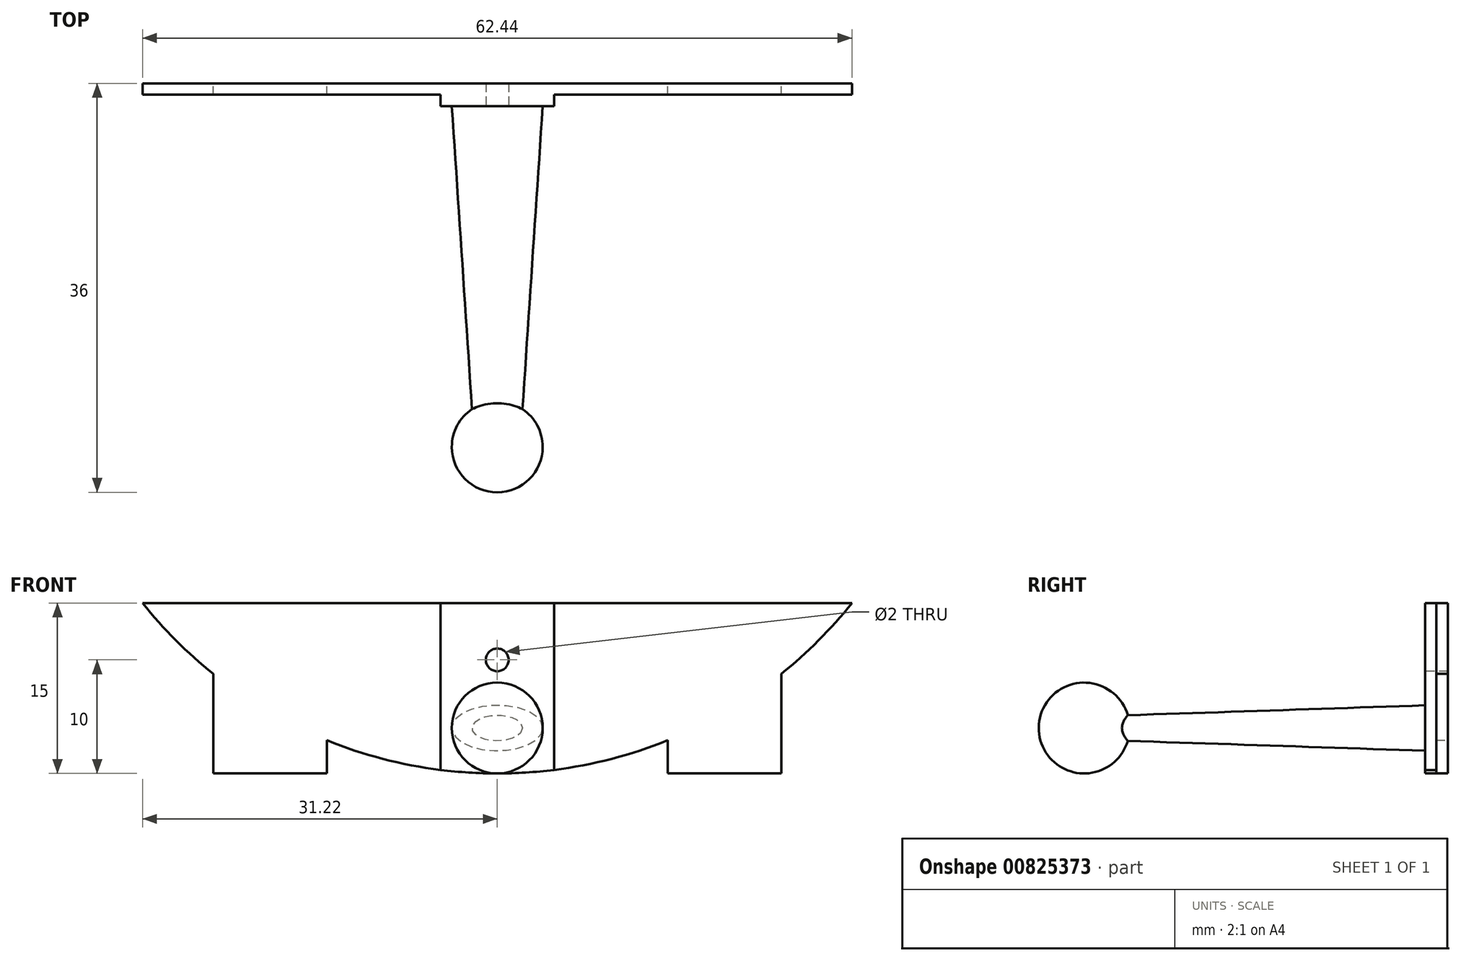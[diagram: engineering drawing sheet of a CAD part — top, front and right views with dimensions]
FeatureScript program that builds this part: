
annotation { "Feature Type Name" : "Feature", "Feature Type Description" : "" }
export const myFeature = defineFeature(function(context is Context, id is Id, definition is map)
    precondition{}
    {
        {
            var Q0;
            Q0=qCreatedBy(makeId("Front.planeOp"),FACE);
            var sketch = newSketch(context, id + "F0", { "sketchPlane" : qUnion([Q0])});
            skArc(sketch, "E0", {"start": v(-31.22, -25) * mm, "mid": v(-28.28, -28.28) * mm, "end": v(-25, -31.22) * mm});
            skLineSegment(sketch, "E1", {"start": v(0, -40) * mm, "end": v(0, -25) * mm, "construction": true});
            skLineSegment(sketch, "E2", {"start": v(0, -25) * mm, "end": v(31.22, -25) * mm});
            skLineSegment(sketch, "E3", {"start": v(0, -25) * mm, "end": v(-31.22, -25) * mm});
            skLineSegment(sketch, "E4", {"start": v(0, -40) * mm, "end": v(15, -40) * mm, "construction": true});
            skLineSegment(sketch, "E5", {"start": v(0, -40) * mm, "end": v(-15, -40) * mm, "construction": true});
            skLineSegment(sketch, "E6", {"start": v(-15, -40) * mm, "end": v(-15, -37.08) * mm});
            skLineSegment(sketch, "E7", {"start": v(15, -40) * mm, "end": v(15, -37.08) * mm});
            skLineSegment(sketch, "E8", {"start": v(15, -40) * mm, "end": v(25, -40) * mm});
            skLineSegment(sketch, "E9", {"start": v(-15, -40) * mm, "end": v(-25, -40) * mm});
            skLineSegment(sketch, "E10", {"start": v(-25, -40) * mm, "end": v(-25, -31.22) * mm});
            skLineSegment(sketch, "E11", {"start": v(25, -40) * mm, "end": v(25, -31.22) * mm});
            skArc(sketch, "E12.trimOffspring", {"start": v(-15, -37.08) * mm, "mid": v(0, -40) * mm, "end": v(15, -37.08) * mm});
            skArc(sketch, "E13.trimOffspring", {"start": v(25, -31.22) * mm, "mid": v(28.28, -28.28) * mm, "end": v(31.22, -25) * mm});
            skSolve(sketch);
        }
        {
            var Q0;
            Q0 = qSketchRegion(id + "F0", true);
            extrude(context, id + "F1", {"entities" : qUnion([Q0]), "depth" : 1 * mm, "offsetDistance" : 25 * mm});
        }
        {
            var Q0;
            Q0=makeQuery(id+"F1.opExtrude","CAP_FACE",FACE,{"disambiguationData":[OSD([sQuery(id+"F0.wireOp",EDGE,"E0"),sQuery(id+"F0.wireOp",EDGE,"E2"),sQuery(id+"F0.wireOp",EDGE,"E3"),sQuery(id+"F0.wireOp",EDGE,"E6"),sQuery(id+"F0.wireOp",EDGE,"E7"),sQuery(id+"F0.wireOp",EDGE,"E8"),sQuery(id+"F0.wireOp",EDGE,"E9"),sQuery(id+"F0.wireOp",EDGE,"E10"),sQuery(id+"F0.wireOp",EDGE,"E11"),sQuery(id+"F0.wireOp",EDGE,"E12.trimOffspring"),sQuery(id+"F0.wireOp",EDGE,"E13.trimOffspring")])],"isStart":false});
            var sketch = newSketch(context, id + "F2", { "sketchPlane" : qUnion([Q0])});
            skLineSegment(sketch, "E14", {"start": v(0, -25) * mm, "end": v(0, -40) * mm, "construction": true});
            skLineSegment(sketch, "E15", {"start": v(0, -25) * mm, "end": v(5, -25) * mm});
            skLineSegment(sketch, "E16", {"start": v(0, -25) * mm, "end": v(-5, -25) * mm});
            skLineSegment(sketch, "E17", {"start": v(-5, -25) * mm, "end": v(-5, -39.69) * mm});
            skLineSegment(sketch, "E18", {"start": v(5, -25) * mm, "end": v(5, -39.69) * mm});
            skArc(sketch, "E19", {"start": v(-5, -39.69) * mm, "mid": v(0, -40) * mm, "end": v(5, -39.69) * mm});
            skSolve(sketch);
        }
        {
            var Q0;
            Q0 = qSketchRegion(id + "F2", true);
            extrude(context, id + "F3", {"entities" : qUnion([Q0]), "operationType" : NewBodyOperationType.ADD, "depth" : 1 * mm, "offsetDistance" : 25 * mm});
        }
        {
            var Q0;
            Q0=makeQuery(id+"F3.opExtrude","CAP_FACE",FACE,{"disambiguationData":[OSD([sQuery(id+"F2.wireOp",EDGE,"E15"),sQuery(id+"F2.wireOp",EDGE,"E16"),sQuery(id+"F2.wireOp",EDGE,"E17"),sQuery(id+"F2.wireOp",EDGE,"E18"),sQuery(id+"F2.wireOp",EDGE,"E19")])],"isStart":false});
            var sketch = newSketch(context, id + "F4", { "sketchPlane" : qUnion([Q0])});
            skLineSegment(sketch, "E20", {"start": v(0, -25) * mm, "end": v(0, -36) * mm, "construction": true});
            skEllipse(sketch, "E21", {"center": v(0, -36) * mm, "majorRadius": 4 * mm, "minorRadius": 2 * mm, "majorAxis": v(1, 0)});
            skSolve(sketch);
        }
        {
            var Q0;
            Q0=qCreatedBy(makeId("Front.planeOp"),FACE);
            cPlane(context, id + "F5", {"entities" : qUnion([Q0]), "cplaneType" : CPlaneType.OFFSET, "offset" : 32 * mm, "width" : 150 * mm, "height" : 150 * mm});
        }
        {
            var Q0;
            Q0=qCreatedBy(id+"F5.planeOp",FACE);
            var sketch = newSketch(context, id + "F6", { "sketchPlane" : qUnion([Q0])});
            skEllipse(sketch, "E22", {"center": v(0, -36) * mm, "majorRadius": 2 * mm, "minorRadius": 1 * mm, "majorAxis": v(1, 0)});
            skSolve(sketch);
        }
        {
            var Q1;
            Q1=makeQuery(id+"F4.imprint","IMPRINT",FACE,{"disambiguationData":[TD([[makeQuery(id+"F4.imprint","IMPRINT",EDGE,{"derivedFrom":sQuery(id+"F4.wireOp",EDGE,"E21")}),1.0]])]});
            var Q2;
            Q2=makeQuery(id+"F6.imprint","IMPRINT",FACE,{"disambiguationData":[TD([[makeQuery(id+"F6.imprint","IMPRINT",EDGE,{"derivedFrom":sQuery(id+"F6.wireOp",EDGE,"E22")}),1.0]])]});
            loft(context, id + "F7", {"operationType" : NewBodyOperationType.ADD, "sheetProfilesArray" : [{ "sheetProfileEntities" : qUnion([Q1]) }, { "sheetProfileEntities" : qUnion([Q2]) }]});
        }
        {
            var Q0;
            Q0=makeQuery(id+"F7.opLoft","CAP_FACE",FACE,{"disambiguationData":[OSD([makeQuery(id+"F6.imprint","IMPRINT",FACE,{"disambiguationData":[TD([[makeQuery(id+"F6.imprint","IMPRINT",EDGE,{"derivedFrom":sQuery(id+"F6.wireOp",EDGE,"E22")}),1.0]])]})])],"isStart":true});
            var sketch = newSketch(context, id + "F8", { "sketchPlane" : qUnion([Q0])});
            skArc(sketch, "E23", {"start": v(4, -36) * mm, "mid": v(0, -32) * mm, "end": v(-4, -36) * mm});
            skLineSegment(sketch, "E24", {"start": v(0, -37) * mm, "end": v(0, -36) * mm, "construction": true});
            skLineSegment(sketch, "E25", {"start": v(-4, -36) * mm, "end": v(4, -36) * mm});
            skSolve(sketch);
        }
        {
            var Q0;
            Q0 = qSketchRegion(id + "F8", true);
            var Q1;
            Q1=sQuery(id+"F8.wireOp",EDGE,"E25");
            revolve(context, id + "F9", {"operationType" : NewBodyOperationType.ADD, "surfaceOperationType" : NewSurfaceOperationType.NEW, "entities" : qUnion([Q0]), "axis" : qUnion([Q1]), "revolveType" : RevolveType.FULL});
        }
        {
            var Q0;
            Q0=makeQuery(id+"F3.opExtrude","CAP_FACE",FACE,{"disambiguationData":[OSD([sQuery(id+"F2.wireOp",EDGE,"E15"),sQuery(id+"F2.wireOp",EDGE,"E16"),sQuery(id+"F2.wireOp",EDGE,"E17"),sQuery(id+"F2.wireOp",EDGE,"E18"),sQuery(id+"F2.wireOp",EDGE,"E19")])],"isStart":false});
            var sketch = newSketch(context, id + "F10", { "sketchPlane" : qUnion([Q0])});
            skLineSegment(sketch, "E26", {"start": v(0, -25) * mm, "end": v(0, -30) * mm, "construction": true});
            skCircle(sketch, "E27", {"center": v(0, -30) * mm, "radius": 1 * mm});
            skSolve(sketch);
        }
        {
            var Q0;
            Q0 = qSketchRegion(id + "F10", true);
            extrude(context, id + "F11", {"entities" : qUnion([Q0]), "operationType" : NewBodyOperationType.REMOVE, "oppositeDirection" : true, "depth" : 25 * mm, "offsetDistance" : 25 * mm});
        }
    });
